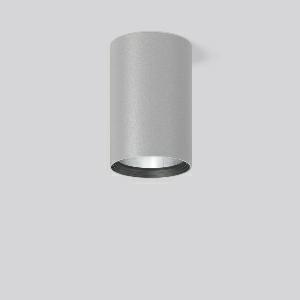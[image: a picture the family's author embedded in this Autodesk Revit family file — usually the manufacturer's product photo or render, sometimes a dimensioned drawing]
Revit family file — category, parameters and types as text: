
# Revit family: heledon_maxi_a_931219_004_1_a9e7
name_source: partatom
category: Lighting Fixtures
units: mm (PartAtom-declared; Revit-internal decimal feet)

## family parameters
Cut with Voids When Loaded = No
Host = Face
Light Source = No
Part Type = Normal
Room Calculation Point = No
Round Connector Dimension = Use Diameter
Shared = No

## types (1)
- HELEDON maxi A (1 x LED Modul 940, 3350 lm, 4000)
    Apparent Load = 25 VA
    Approval mark = CE
    CIE Flux Codes = 97 100 100 100 100
    Color Rendering = 92
    Color Temperature = 4000
    Default Elevation = 1800 mm
    Description = Series: HELEDON maxi
Cylindrical surface-mounted downlight. Housing: die-cast aluminium, powder-coated. Internal ceiling frame polycarbonate with bayonet mounting. Black plastic ring and recessed LED to prevent glare from the side. Optical assembly with reflector made of MIRO-Silver with 98% total light reflection for outstanding efficiency - can be changed without tools. Best colour rendering index Ra>90. Suitable for Ceiling mounting. Easy installation with a separate ceiling frame with bayonet mounting and plug connection. Driver integrated. Connected via plug-in connector. High quality converter without flickering and stroboscopic effect. The following accessories can be mounted without use of tools: interchangeable lenses, decorative glasses, honeycomb louvre, clear and frosted diffusers, white interchangeable plastic ring. 
Colour: silver
Diameter: 123 mm
Height: 183 mm
Lamp: LED
Socket: without socket
Colour temperature: 4000K
Colour rendering index (CRI): 92
System power: 25 W
Rated luminous flux: 3350 lm
Luminous efficiency: 134 lm/W
Control gear: Regulated power supply
Protection class: I
Type of protection: IP 20
    Height = 183 mm
    Lamp = 1 x LED Modul 940
    Lamp Light Flux = 3350 lm
    Lamp count = 1
    Length = 123 mm
    Lifetime = 50000 h
    Luminous efficacy = 134 lm/W
    Manufacturer = RZB
    ModVariant = No
    Model = 931219.004.1
    Mounting Place = Ceiling
    Mounting Type = Surface mounted
    Number of Poles = 1
    OnlyDefault = Yes
    Power Factor = 1
    Product Name = HELEDON maxi A
    Product group = Surface mounted downlights
    ProductGroupID = 302
    Protection Class = Protection class I
    Protection Degree = IP 20
    RLX_Detail_Level = 1
    RLX_Emergency_Light_Flux = 0 lm
    RLX_Emergency_Type = 0
    RLX_Emergency_Type_DB = No
    RlxData = <blob elided: 100473 chars, md5=6c348766>
    Socket = socket
    Standby Power = 0 W
    System Light Flux = 3350 lm
    System Power = 25 W
    Type Comments = Product without accessories
    Type Image = 931192.004.jpg
    URL = http://relux.com
    VarID = ---
    Voltage = 230 V
    Voltage Range = 220-240 V
    Weight = 0.00 kg
    Width = 0 mm  [stored 0 ft]

note: [stored X ft] marks values corroborated as IEEE doubles in the binary element streams (Revit-internal decimal feet)

## geometry (parser evidence)
native form markers: Blend x4, Sweep x11
no freeform markers — native parametric forms only
